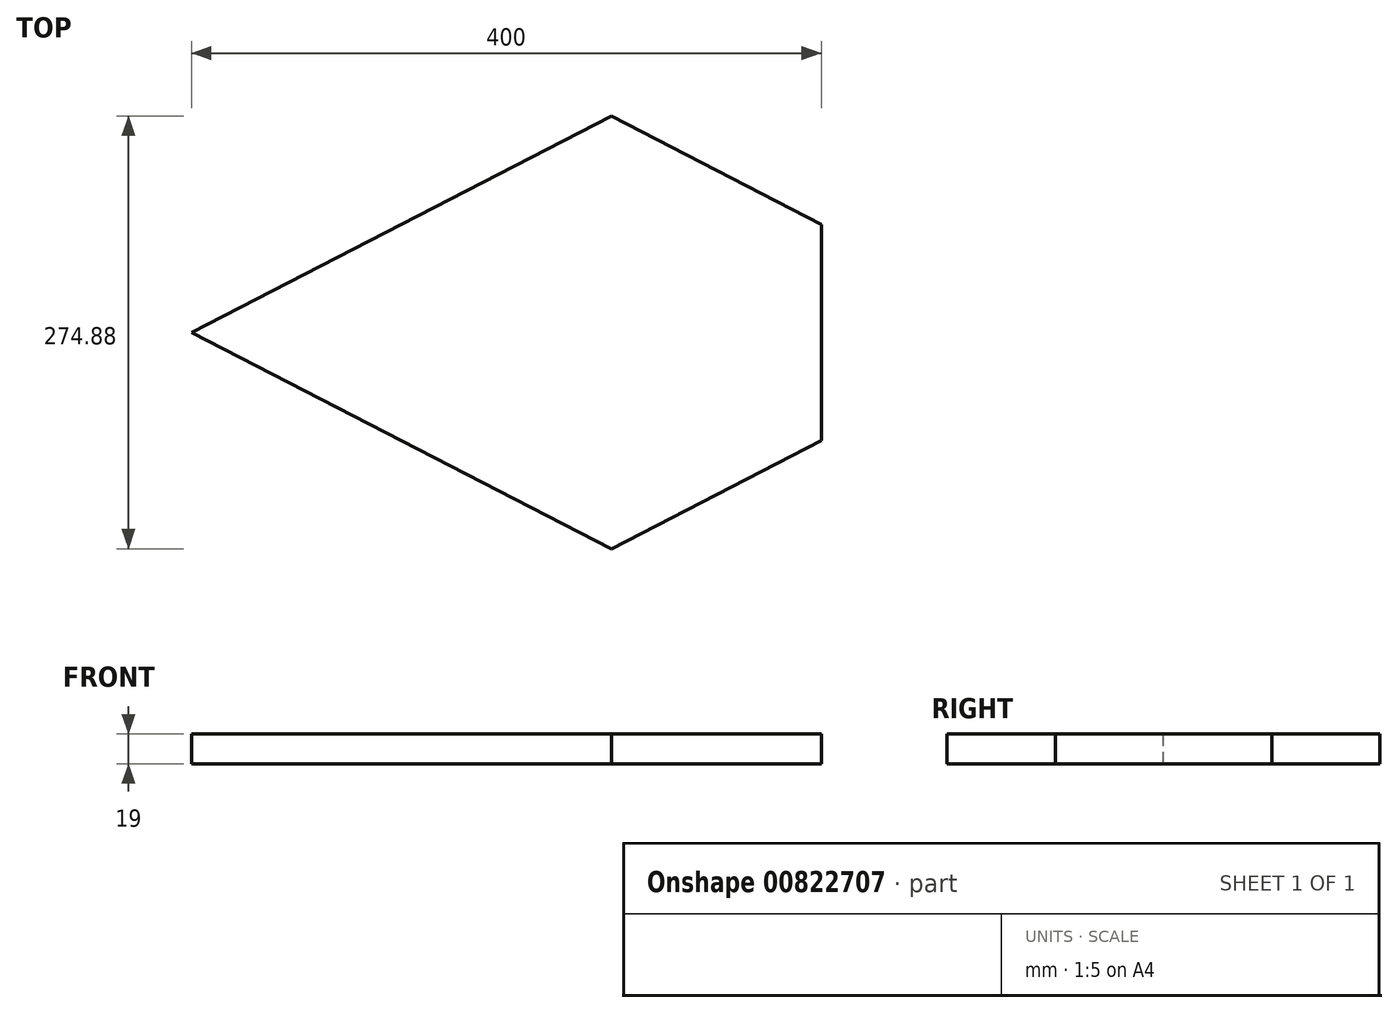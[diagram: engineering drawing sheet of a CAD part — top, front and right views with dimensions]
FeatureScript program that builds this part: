
annotation { "Feature Type Name" : "Feature", "Feature Type Description" : "" }
export const myFeature = defineFeature(function(context is Context, id is Id, definition is map)
    precondition{}
    {
        {
            var Q0;
            Q0=qCreatedBy(makeId("Top.planeOp"),FACE);
            var sketch = newSketch(context, id + "F0", { "sketchPlane" : qUnion([Q0])});
            skLineSegment(sketch, "E0.bottom", {"start": v(-200, 175) * mm, "end": v(200, 175) * mm});
            skLineSegment(sketch, "E0.top", {"start": v(-200, -175) * mm, "end": v(200, -175) * mm});
            skLineSegment(sketch, "E0.left", {"start": v(-200, 175) * mm, "end": v(-200, -175) * mm});
            skLineSegment(sketch, "E0.right", {"start": v(200, 175) * mm, "end": v(200, -175) * mm});
            skPoint(sketch, "E0.middle", {"position": v(0, 0) * mm});
            skSolve(sketch);
        }
        {
            var Q0;
            Q0 = qSketchRegion(id + "F0", true);
            extrude(context, id + "F1", {"entities" : qUnion([Q0]), "depth" : 19 * mm, "offsetDistance" : 25 * mm});
        }
        {
            var Q0;
            Q0=makeQuery(id+"F1.opExtrude","CAP_FACE",FACE,{"disambiguationData":[OSD([sQuery(id+"F0.wireOp",EDGE,"E0.bottom"),sQuery(id+"F0.wireOp",EDGE,"E0.top"),sQuery(id+"F0.wireOp",EDGE,"E0.left"),sQuery(id+"F0.wireOp",EDGE,"E0.right")])],"isStart":false});
            var sketch = newSketch(context, id + "F2", { "sketchPlane" : qUnion([Q0])});
            skLineSegment(sketch, "E1", {"start": v(-200, 0) * mm, "end": v(66.67, -137.44) * mm});
            skLineSegment(sketch, "E2", {"start": v(66.67, -137.44) * mm, "end": v(200, -68.72) * mm});
            skLineSegment(sketch, "E3", {"start": v(-200, 0) * mm, "end": v(66.67, 137.44) * mm});
            skLineSegment(sketch, "E4", {"start": v(66.67, 137.44) * mm, "end": v(200, 68.72) * mm});
            skLineSegment(sketch, "E5", {"start": v(200, 68.72) * mm, "end": v(200, -68.72) * mm});
            skLineSegment(sketch, "E6", {"start": v(-200, 0) * mm, "end": v(200, 0) * mm});
            skLineSegment(sketch, "E7", {"start": v(-138.24, 0) * mm, "end": v(39.54, -91.62) * mm});
            skLineSegment(sketch, "E8", {"start": v(39.54, -91.62) * mm, "end": v(131.76, 0) * mm});
            skLineSegment(sketch, "E9", {"start": v(-138.24, 0) * mm, "end": v(39.54, 91.62) * mm});
            skLineSegment(sketch, "E10", {"start": v(39.54, 91.62) * mm, "end": v(131.76, 0) * mm});
            skSolve(sketch);
        }
        {
            var Q0;
            {var subQ2=sQuery(id+"F2.wireOp",EDGE,"E1");Q0=makeQuery(id+"F2.imprint","IMPRINT",FACE,{"disambiguationData":[TD([[makeQuery(id+"F2.imprint","IMPRINT",EDGE,{"derivedFrom":subQ2}),-1.0]])]});}
            extrude(context, id + "F3", {"entities" : qUnion([Q0]), "operationType" : NewBodyOperationType.REMOVE, "endBound" : BoundingType.THROUGH_ALL, "oppositeDirection" : true, "depth" : 25 * mm, "offsetDistance" : 25 * mm});
        }
        {
            var Q0;
            {var subQ2=sQuery(id+"F2.wireOp",EDGE,"E3");Q0=makeQuery(id+"F2.imprint","IMPRINT",FACE,{"disambiguationData":[TD([[makeQuery(id+"F2.imprint","IMPRINT",EDGE,{"derivedFrom":subQ2}),1.0]])]});}
            extrude(context, id + "F4", {"entities" : qUnion([Q0]), "operationType" : NewBodyOperationType.REMOVE, "endBound" : BoundingType.THROUGH_ALL, "oppositeDirection" : true, "depth" : 25 * mm, "offsetDistance" : 25 * mm});
        }
    });
